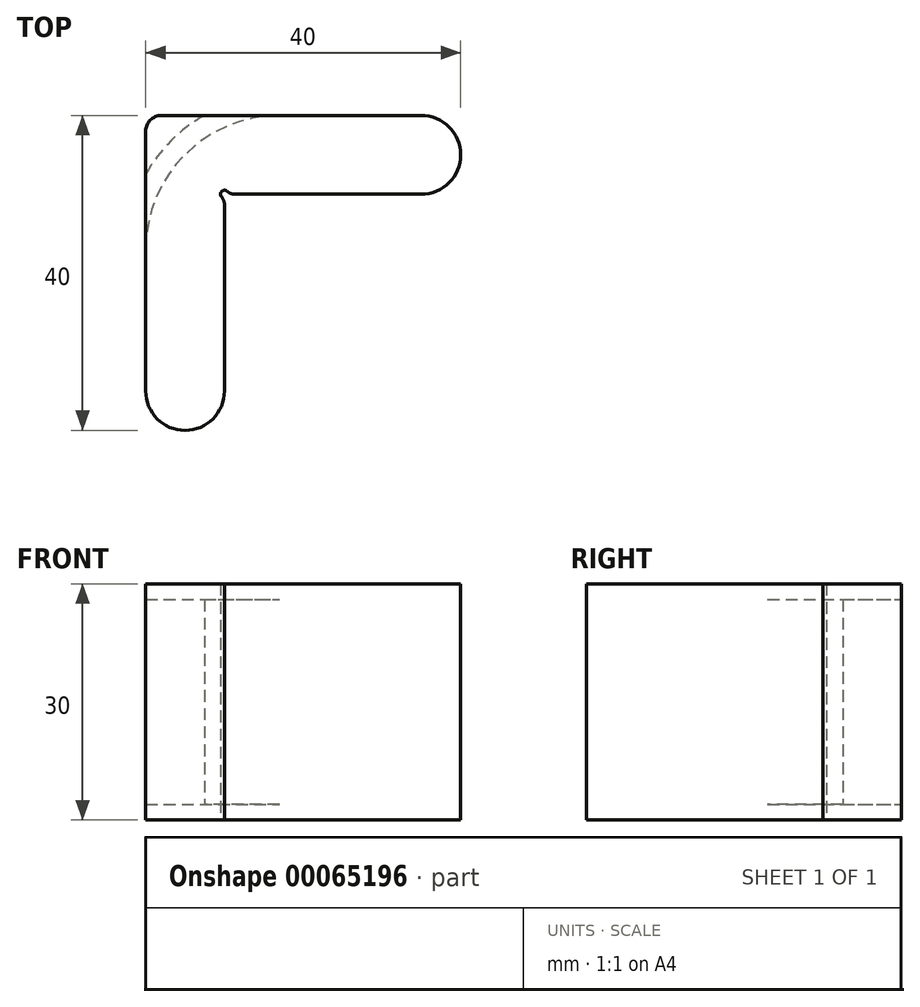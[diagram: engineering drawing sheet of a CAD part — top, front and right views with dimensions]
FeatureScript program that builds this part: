
annotation { "Feature Type Name" : "Feature", "Feature Type Description" : "" }
export const myFeature = defineFeature(function(context is Context, id is Id, definition is map)
    precondition{}
    {
        {
            var Q0;
            Q0=qCreatedBy(makeId("Top.planeOp"),FACE);
            var sketch = newSketch(context, id + "F0", { "sketchPlane" : qUnion([Q0])});
            skLineSegment(sketch, "E0.rect.bottom", {"start": v(-15, 20) * mm, "end": v(15, 20) * mm});
            skLineSegment(sketch, "E0.rect.top", {"start": v(-15, -20) * mm, "end": v(-15, -20) * mm});
            skLineSegment(sketch, "E0.rect.left", {"start": v(-20, 15) * mm, "end": v(-20, -15) * mm});
            skLineSegment(sketch, "E0.rect.right", {"start": v(20, 15) * mm, "end": v(20, 15) * mm});
            skPoint(sketch, "E0.rect.middle", {"position": v(0, 0) * mm});
            skLineSegment(sketch, "E1.0", {"start": v(-9.5, 10) * mm, "end": v(15, 10) * mm});
            skLineSegment(sketch, "E1.1", {"start": v(-10, 9.5) * mm, "end": v(-10, -15) * mm});
            skPoint(sketch, "E2.orphan", {"position": v(20, -20) * mm});
            skPoint(sketch, "E3.visualSharp", {"position": v(-20, -20) * mm});
            skArc(sketch, "E3.filletArc", {"start": v(-20, -15) * mm, "mid": v(-18.54, -18.54) * mm, "end": v(-15, -20) * mm});
            skPoint(sketch, "E4.visualSharp", {"position": v(-10, -20) * mm});
            skArc(sketch, "E4.filletArc", {"start": v(-15, -20) * mm, "mid": v(-11.46, -18.54) * mm, "end": v(-10, -15) * mm});
            skPoint(sketch, "E5.visualSharp", {"position": v(20, 10) * mm});
            skArc(sketch, "E5.filletArc", {"start": v(15, 10) * mm, "mid": v(18.54, 11.46) * mm, "end": v(20, 15) * mm});
            skPoint(sketch, "E6.visualSharp", {"position": v(20, 20) * mm});
            skArc(sketch, "E6.filletArc", {"start": v(20, 15) * mm, "mid": v(18.54, 18.54) * mm, "end": v(15, 20) * mm});
            skPoint(sketch, "E7.visualSharp", {"position": v(-20, 20) * mm});
            skArc(sketch, "E8", {"start": v(-10, 9.5) * mm, "mid": v(-10.35, 10.35) * mm, "end": v(-9.5, 10) * mm});
            skLineSegment(sketch, "E9", {"start": v(-20, 15) * mm, "end": v(-20, 18) * mm});
            skLineSegment(sketch, "E10", {"start": v(-18, 20) * mm, "end": v(-15, 20) * mm});
            skArc(sketch, "E11.filletArc", {"start": v(-18, 20) * mm, "mid": v(-19.41, 19.41) * mm, "end": v(-20, 18) * mm});
            skSolve(sketch);
        }
        {
            var Q0;
            Q0=makeQuery(id+"F0.imprint","IMPRINT",FACE,{"disambiguationData":[TD([[makeQuery(id+"F0.imprint","IMPRINT",EDGE,{"derivedFrom":sQuery(id+"F0.wireOp",EDGE,"E0.rect.bottom")}),-1.0]])]});
            extrude(context, id + "F1", {"entities" : qUnion([Q0]), "depth" : 30 * mm});
        }
        {
            var Q0;
            Q0=makeQuery(id+"F1.opExtrude","CAP_FACE",FACE,{"disambiguationData":[OSD([sQuery(id+"F0.wireOp",EDGE,"E0.rect.bottom"),sQuery(id+"F0.wireOp",EDGE,"E0.rect.left"),sQuery(id+"F0.wireOp",EDGE,"E1.0"),sQuery(id+"F0.wireOp",EDGE,"E1.1"),sQuery(id+"F0.wireOp",EDGE,"E3.filletArc"),sQuery(id+"F0.wireOp",EDGE,"E4.filletArc"),sQuery(id+"F0.wireOp",EDGE,"E5.filletArc"),sQuery(id+"F0.wireOp",EDGE,"E6.filletArc"),sQuery(id+"F0.wireOp",EDGE,"E7.filletArc"),sQuery(id+"F0.wireOp",EDGE,"E8")])],"isStart":false});
            var sketch = newSketch(context, id + "F2", { "sketchPlane" : qUnion([Q0])});
            skLineSegment(sketch, "E12", {"start": v(-20, 3) * mm, "end": v(-5.61, 17.39) * mm});
            skArc(sketch, "E13", {"start": v(-3, 20) * mm, "mid": v(-15.02, 15.02) * mm, "end": v(-20, 3) * mm});
            skPoint(sketch, "E13.second.point", {"position": v(-3, 20) * mm});
            skPoint(sketch, "E13.third.point", {"position": v(2.44, 19.1) * mm});
            skPoint(sketch, "E14.0", {"position": v(-20, 18) * mm});
            skSolve(sketch);
        }
        {
            var Q0;
            Q0=sQuery(id+"F2.wireOp",VERTEX,"E13.end");
            var Q1;
            Q1=makeQuery(id+"F1.opExtrude","CAP_EDGE",EDGE,{"disambiguationData":[OSD([sQuery(id+"F0.wireOp",EDGE,"E0.rect.left")])],"isStart":false});
            cPlane(context, id + "F3", {"entities" : qUnion([Q0, Q1]), "cplaneType" : CPlaneType.LINE_POINT, "offset" : 150 * mm, "width" : 150 * mm, "height" : 150 * mm});
        }
        {
            var Q0;
            Q0=qCreatedBy(id+"F3.planeOp",FACE);
            var sketch = newSketch(context, id + "F4", { "sketchPlane" : qUnion([Q0])});
            skPoint(sketch, "E15.0", {"position": v(22.5, 30) * mm});
            skLineSegment(sketch, "E16", {"start": v(22.5, 30) * mm, "end": v(22.5, 0) * mm});
            skPoint(sketch, "E17.rect.middle", {"position": v(22.5, 15) * mm});
            skLineSegment(sketch, "E18.bottom", {"start": v(22.5, 28) * mm, "end": v(20, 28) * mm});
            skLineSegment(sketch, "E18.top", {"start": v(22.5, 2) * mm, "end": v(20, 2) * mm});
            skLineSegment(sketch, "E18.left", {"start": v(22.5, 33) * mm, "end": v(22.5, 2) * mm});
            skLineSegment(sketch, "E18.right", {"start": v(20, 28) * mm, "end": v(20, 2) * mm});
            skPoint(sketch, "E19", {"position": v(20, 15) * mm});
            skPoint(sketch, "E20.0", {"position": v(20, 30) * mm});
            skLineSegment(sketch, "E21", {"start": v(20, 30) * mm, "end": v(20, 0) * mm});
            skSolve(sketch);
        }
        {
            var Q0;
            Q0=makeQuery(id+"F4.imprint","IMPRINT",FACE,{"disambiguationData":[TD([[makeQuery(id+"F4.imprint","IMPRINT",EDGE,{"derivedFrom":sQuery(id+"F4.wireOp",EDGE,"E18.bottom")}),1.0]])]});
            var Q1;
            Q1=sQuery(id+"F2.wireOp",EDGE,"E13");
            sweep(context, id + "F5", {"operationType" : NewBodyOperationType.REMOVE, "profiles" : qUnion([Q0]), "path" : qUnion([Q1])});
        }
        {
            var Q0;
            Q0=makeQuery(id+"F1.opExtrude","SWEPT_EDGE",EDGE,{"disambiguationData":[OSD([sQuery(id+"F0.wireOp",EDGE,"E1.1"),sQuery(id+"F0.wireOp",EDGE,"E8")])]});
            var Q1;
            Q1=makeQuery(id+"F1.opExtrude","SWEPT_EDGE",EDGE,{"disambiguationData":[OSD([sQuery(id+"F0.wireOp",EDGE,"E1.0"),sQuery(id+"F0.wireOp",EDGE,"E8")])]});
            fillet(context, id + "F6", {"entities" : qUnion([Q0, Q1]), "radius" : 1.5 * mm, "allowEdgeOverflow" : false});
        }
    });
